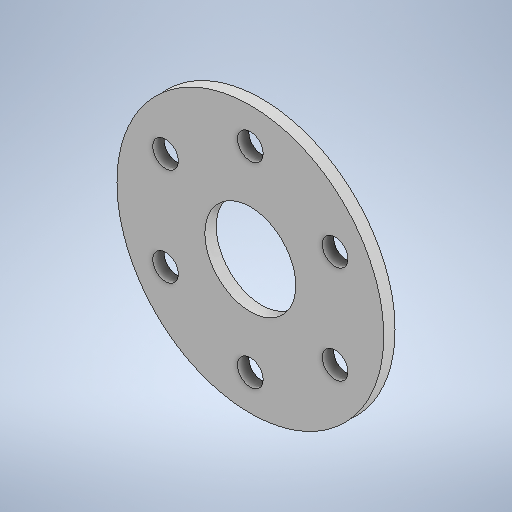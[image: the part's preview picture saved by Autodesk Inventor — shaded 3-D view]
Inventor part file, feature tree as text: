
AUTODESK INVENTOR PART (.ipt)
format: ipt  version: 2025.2 (Build 292293000, 293)  size: 244,224 bytes
history: native  units: mm
features: sketch x2, extrude x1
ambient origin geometry x8: Origin, YZ Plane, XZ Plane, XY Plane, X Axis, Y Axis, Z Axis, Center Point
bodies: Solid1 (feature_tree)
feature tree (3):
  extrude  "Extrusion1"  Depth=34.5mm
  sketch  "Sketch1"  dims[d0=47.0mm d1=34.5mm]
  sketch  "Sketch Circular Pattern1"  dims[d2=4.5mm d3=60.0mm d5=360.0deg d7=16.0mm d8=2.0mm d9=0.0mm]
